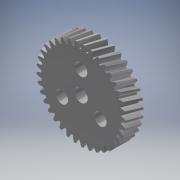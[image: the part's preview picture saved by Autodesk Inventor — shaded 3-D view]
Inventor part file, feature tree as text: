
AUTODESK INVENTOR PART (.ipt)
format: ipt  version: 2019 (Build 230136000, 136)  size: 606,208 bytes
history: native  units: mm (DEFAULTED — no unit token found)
features: sketch x4, plane x3, other x3, extrude x2, hole x1
ambient origin geometry x8: Origin, YZ Plane, XZ Plane, XY Plane, X Axis, Y Axis, Z Axis, Center Point
bodies: Solid1 (feature_tree)
feature tree (13):
  extrude  "Extrusion1"  Depth=10.0mm TaperAngle=0.0deg
  plane  "Work Plane2"
  plane  "Work Plane8"
  plane  "Work Plane9"
  other  "Spur Gear"
  extrude  "Extrusion2"  Depth=10.0mm TaperAngle=0.0deg
  hole  "Hole1"  [1 undecoded]
  sketch  "Sketch1"  dims[d0=50.240958mm d1=10.0mm d2=0.0mm]
  sketch  "Sketch2"  dims[d3=47.741935mm d4=10.0mm d5=0.0mm]
  other  "Srf1"
  sketch  "Sketch3"  dims[d16=40.0mm d17=0.0mm d34=0.849079mm]
  sketch  "Sketch4"  dims[d39=0.0mm d41=0.0mm d43=40.0mm d46=40.0mm d47=0.0mm d48=0.0mm d49=7.5mm d50=10.0mm d51=0.0mm d52=25.0mm d53=30.0mm d55=360.0deg d57=5.0mm d58=6.0mm d59=7.0mm d60=5.0mm d61=90.0deg d62=8.0mm d63=90.0deg]
  other  "Pitch Diameter"
note: 1 required parameter value undecoded (feature->parameter linkage not recoverable at this tier; creation-order binding heuristic only, values carry confidence <= 0.55)
